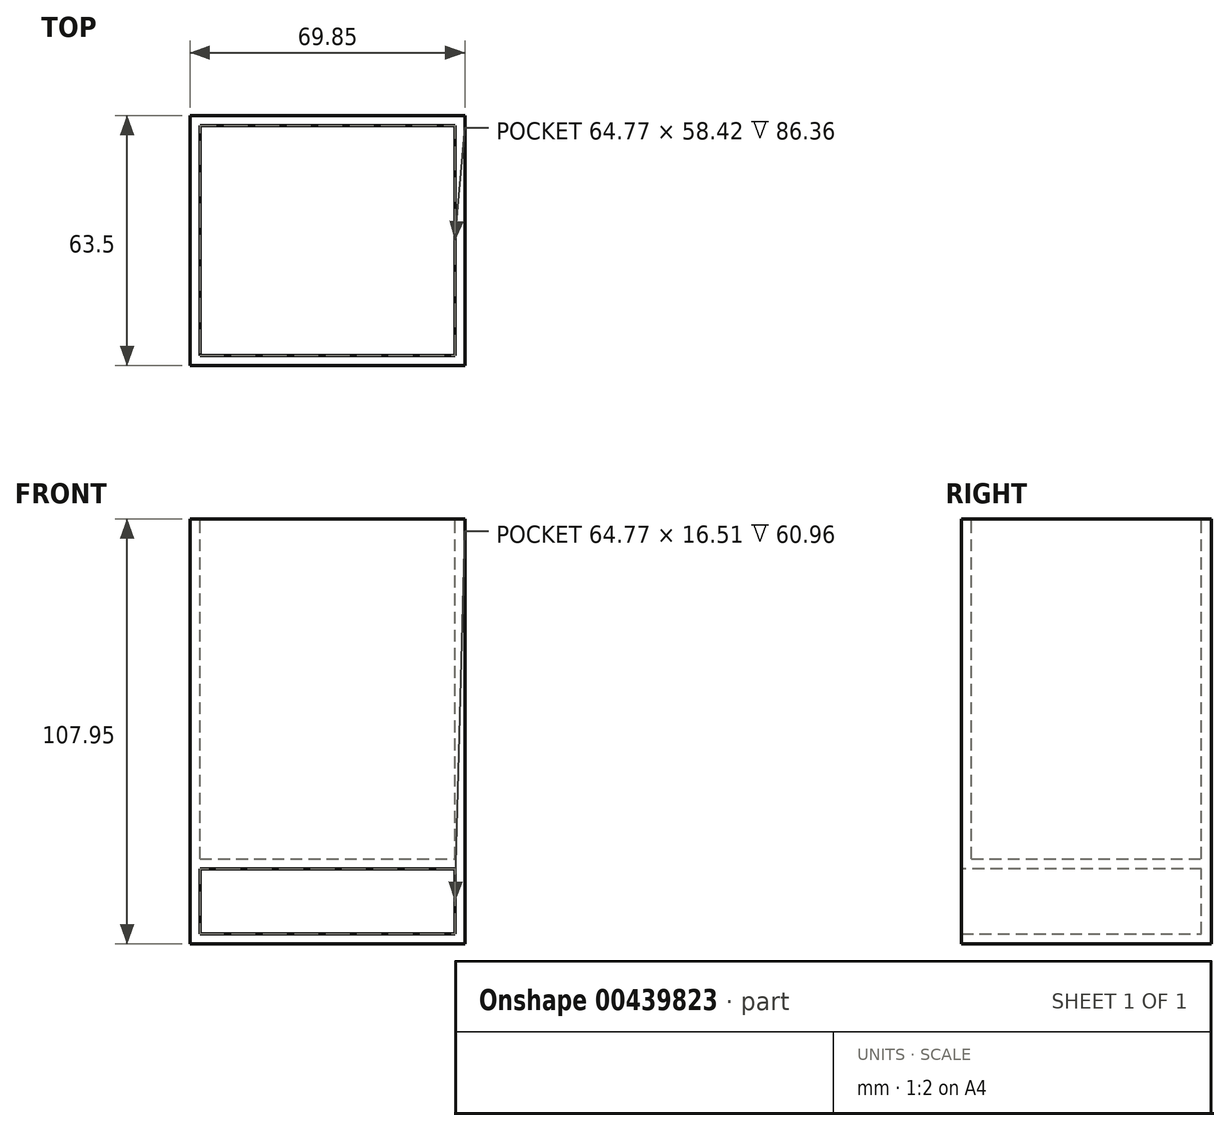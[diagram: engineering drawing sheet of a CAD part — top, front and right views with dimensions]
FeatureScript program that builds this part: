
annotation { "Feature Type Name" : "Feature", "Feature Type Description" : "" }
export const myFeature = defineFeature(function(context is Context, id is Id, definition is map)
    precondition{}
    {
        {
            var Q0;
            Q0=qCreatedBy(makeId("Front.planeOp"),FACE);
            var sketch = newSketch(context, id + "F0", { "sketchPlane" : qUnion([Q0])});
            skLineSegment(sketch, "E0", {"start": v(-57.46, 46.55) * mm, "end": v(-57.46, -65.6) * mm});
            skLineSegment(sketch, "E1", {"start": v(-57.46, -65.6) * mm, "end": v(47.64, -65.6) * mm});
            skLineSegment(sketch, "E2", {"start": v(47.64, -65.6) * mm, "end": v(47.64, 46.55) * mm});
            skLineSegment(sketch, "E3", {"start": v(47.64, 46.55) * mm, "end": v(-57.46, 46.55) * mm});
            skLineSegment(sketch, "E4.bottom", {"start": v(-44.64, -46.54) * mm, "end": v(25.2, -46.54) * mm});
            skLineSegment(sketch, "E4.top", {"start": v(-44.64, 42.36) * mm, "end": v(25.2, 42.36) * mm});
            skLineSegment(sketch, "E4.left", {"start": v(-44.64, -46.54) * mm, "end": v(-44.64, 42.36) * mm});
            skLineSegment(sketch, "E4.right", {"start": v(25.2, -46.54) * mm, "end": v(25.2, 42.36) * mm});
            skLineSegment(sketch, "E5", {"start": v(-44.64, -46.54) * mm, "end": v(-44.64, -65.6) * mm});
            skPoint(sketch, "E5.endSnap0", {"position": v(-4.9, -65.6) * mm});
            skLineSegment(sketch, "E6", {"start": v(-44.64, -65.6) * mm, "end": v(25.2, -65.6) * mm});
            skLineSegment(sketch, "E7", {"start": v(25.2, -65.6) * mm, "end": v(25.2, -46.54) * mm});
            skSolve(sketch);
        }
        {
            var Q0;
            Q0=makeQuery(id+"F0.imprint","IMPRINT",FACE,{"disambiguationData":[TD([[makeQuery(id+"F0.imprint","IMPRINT",EDGE,{"derivedFrom":sQuery(id+"F0.wireOp",EDGE,"E4.bottom")}),1.0]])]});
            extrude(context, id + "F1", {"entities" : qUnion([Q0]), "depth" : 63.5 * mm});
        }
        {
            var Q0;
            Q0=makeQuery(id+"F1.opExtrude","SWEPT_FACE",FACE,{"disambiguationData":[OSD([sQuery(id+"F0.wireOp",EDGE,"E4.top")])]});
            shell(context, id + "F2", {"entities" : qUnion([Q0]), "thickness" : 2.54 * mm});
        }
        {
            var Q0;
            Q0=makeQuery(id+"F0.imprint","IMPRINT",FACE,{"disambiguationData":[TD([[makeQuery(id+"F0.imprint","IMPRINT",EDGE,{"derivedFrom":sQuery(id+"F0.wireOp",EDGE,"E4.bottom")}),-1.0]])]});
            extrude(context, id + "F3", {"entities" : qUnion([Q0]), "operationType" : NewBodyOperationType.ADD, "depth" : 63.5 * mm});
        }
        {
            var Q0;
            {var subQ0=sQuery(id+"F0.wireOp",EDGE,"E4.bottom");Q0=makeQuery(id+"F3.boolean.opBoolean","MERGE",FACE,{"derivedFrom":[makeQuery(id+"F1.opExtrude","CAP_FACE",FACE,{"disambiguationData":[OSD([subQ0,sQuery(id+"F0.wireOp",EDGE,"E4.top"),sQuery(id+"F0.wireOp",EDGE,"E4.left"),sQuery(id+"F0.wireOp",EDGE,"E4.right")])],"isStart":false}),makeQuery(id+"F3.opExtrude","CAP_FACE",FACE,{"disambiguationData":[OSD([subQ0,sQuery(id+"F0.wireOp",EDGE,"E5"),sQuery(id+"F0.wireOp",EDGE,"E6"),sQuery(id+"F0.wireOp",EDGE,"E7")])],"isStart":false})]});}
            shell(context, id + "F4", {"entities" : qUnion([Q0]), "thickness" : 2.54 * mm});
        }
    });
